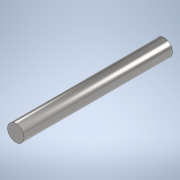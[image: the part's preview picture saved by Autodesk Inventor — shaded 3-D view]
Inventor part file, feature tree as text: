
AUTODESK INVENTOR PART (.ipt)
format: ipt  version: 2021.1 (Build 251245010, 245A)  size: 97,792 bytes
history: native  units: in
note: dims shown in document units (in); Inventor stores cm internally (conversion verified against a paired STEP export)
features: extrude x1, sketch x1
ambient origin geometry x8: Origin, YZ Plane, XZ Plane, XY Plane, X Axis, Y Axis, Z Axis, Center Point
bodies: Solid1 (feature_tree)
feature tree (2):
  extrude  "Extrusion1"  Depth=5.6in TaperAngle=0.0deg
  sketch  "Sketch1"  dims[d0=0.625in d1=5.6in d2=0.0in]
